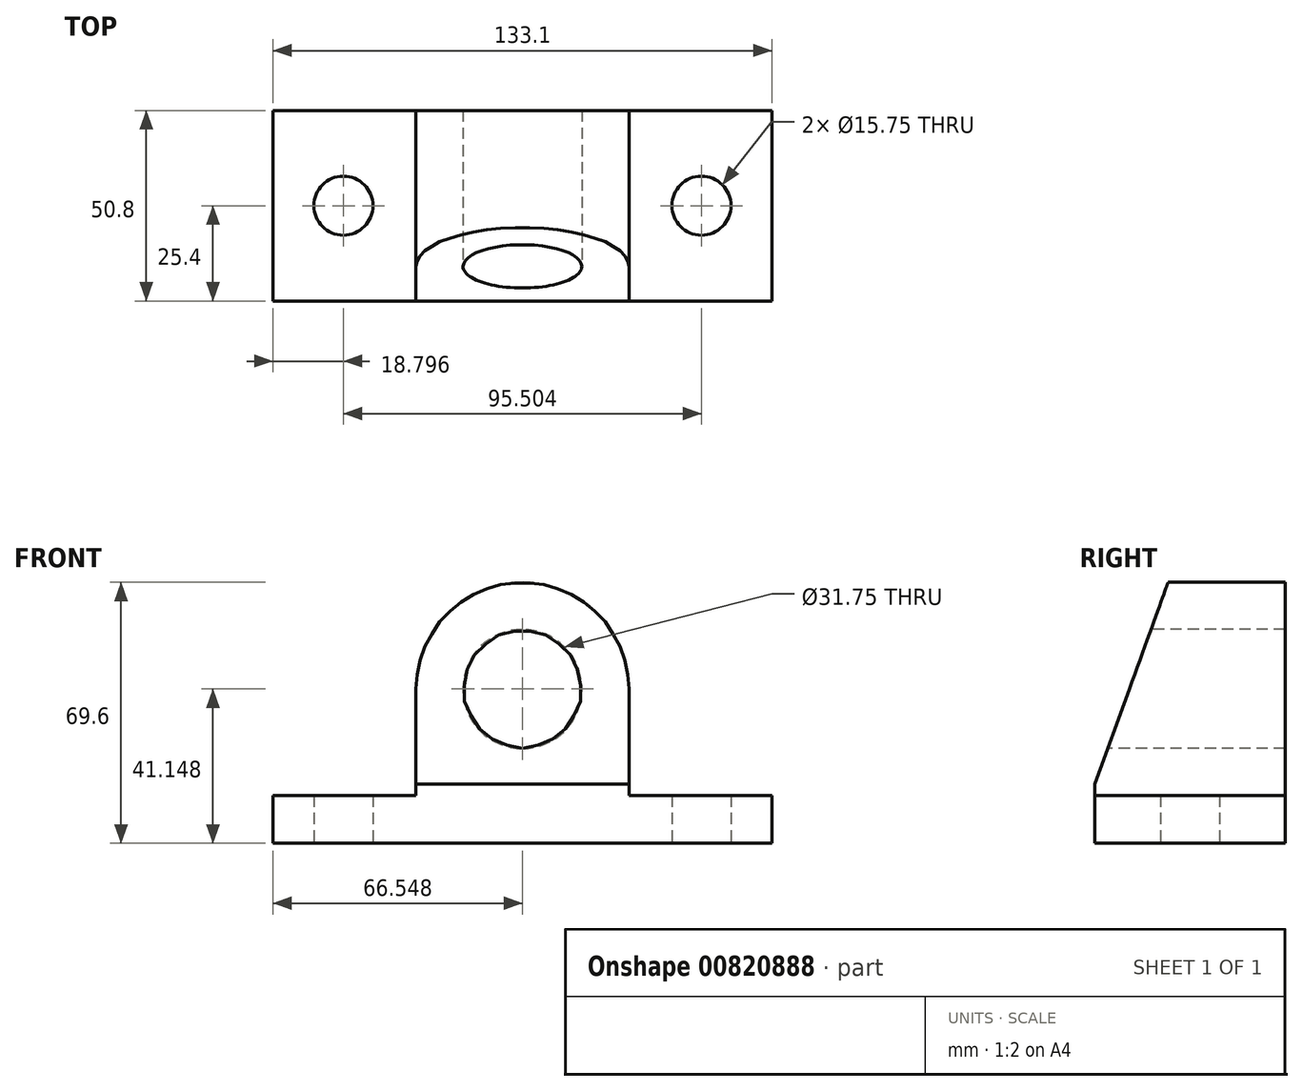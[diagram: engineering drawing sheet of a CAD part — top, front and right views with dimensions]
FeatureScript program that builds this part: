
annotation { "Feature Type Name" : "Feature", "Feature Type Description" : "" }
export const myFeature = defineFeature(function(context is Context, id is Id, definition is map)
    precondition{}
    {
        {
            var Q0;
            Q0=qCreatedBy(makeId("Top.planeOp"),FACE);
            var sketch = newSketch(context, id + "F0", { "sketchPlane" : qUnion([Q0])});
            skLineSegment(sketch, "E0.bottom", {"start": v(0, 0) * mm, "end": v(133.1, 0) * mm});
            skLineSegment(sketch, "E0.top", {"start": v(0, 50.8) * mm, "end": v(133.1, 50.8) * mm});
            skLineSegment(sketch, "E0.left", {"start": v(0, 0) * mm, "end": v(0, 50.8) * mm});
            skLineSegment(sketch, "E0.right", {"start": v(133.1, 0) * mm, "end": v(133.1, 50.8) * mm});
            skLineSegment(sketch, "E1", {"start": v(0, 50.8) * mm, "end": v(66.55, 50.8) * mm});
            skCircle(sketch, "E2", {"center": v(18.8, 25.4) * mm, "radius": 7.87 * mm});
            skCircle(sketch, "E3", {"center": v(114.3, 25.4) * mm, "radius": 7.87 * mm});
            skPoint(sketch, "E4.end.orphan", {"position": v(66.55, 0) * mm});
            skPoint(sketch, "E4.start.orphan", {"position": v(66.55, 25.4) * mm});
            skSolve(sketch);
        }
        {
            var Q0;
            Q0=makeQuery(id+"F0.imprint","IMPRINT",FACE,{"disambiguationData":[TD([[makeQuery(id+"F0.imprint","IMPRINT",EDGE,{"derivedFrom":sQuery(id+"F0.wireOp",EDGE,"E0.bottom")}),1.0]])]});
            extrude(context, id + "F1", {"entities" : qUnion([Q0]), "depth" : 152.4 * mm, "offsetDistance" : 25.4 * mm});
        }
        {
            var Q0;
            Q0=makeQuery(id+"F1.opExtrude","SWEPT_FACE",FACE,{"disambiguationData":[OSD([sQuery(id+"F0.wireOp",EDGE,"E0.bottom")])]});
            var sketch = newSketch(context, id + "F2", { "sketchPlane" : qUnion([Q0])});
            skLineSegment(sketch, "E5", {"start": v(0, 0) * mm, "end": v(0, 12.7) * mm});
            skLineSegment(sketch, "E6", {"start": v(0, 12.7) * mm, "end": v(133.1, 12.7) * mm});
            skLineSegment(sketch, "E7", {"start": v(133.1, 12.7) * mm, "end": v(133.1, 0) * mm});
            skCircle(sketch, "E8", {"center": v(66.55, 41.15) * mm, "radius": 15.88 * mm});
            skLineSegment(sketch, "E9", {"start": v(38.1, 41.15) * mm, "end": v(38.1, 12.7) * mm});
            skLineSegment(sketch, "E10", {"start": v(95, 41.15) * mm, "end": v(95, 12.7) * mm});
            skLineSegment(sketch, "E11", {"start": v(38.1, 12.7) * mm, "end": v(38.1, 15.75) * mm});
            skLineSegment(sketch, "E12", {"start": v(38.1, 15.75) * mm, "end": v(95, 15.75) * mm});
            skArc(sketch, "E13.trimOffspring", {"start": v(95, 41.15) * mm, "mid": v(66.55, 69.6) * mm, "end": v(38.1, 41.15) * mm});
            skPoint(sketch, "E14.start.orphan", {"position": v(66.55, 12.7) * mm});
            skSolve(sketch);
        }
        {
            var Q0;
            Q0=makeQuery(id+"F2.imprint","IMPRINT",FACE,{"disambiguationData":[TD([[makeQuery(id+"F2.imprint","IMPRINT",EDGE,{"derivedFrom":sQuery(id+"F2.wireOp",EDGE,"E9")}),-1.0]])]});
            var Q1;
            Q1=makeQuery(id+"F2.imprint","IMPRINT",FACE,{"disambiguationData":[TD([[makeQuery(id+"F2.imprint","IMPRINT",EDGE,{"derivedFrom":sQuery(id+"F2.wireOp",EDGE,"E8")}),1.0]])]});
            extrude(context, id + "F3", {"entities" : qUnion([Q0, Q1]), "operationType" : NewBodyOperationType.REMOVE, "oppositeDirection" : true, "depth" : 173.74 * mm, "offsetDistance" : 25.4 * mm});
        }
        {
            var Q0;
            Q0=qCreatedBy(makeId("Right.planeOp"),FACE);
            var sketch = newSketch(context, id + "F4", { "sketchPlane" : qUnion([Q0])});
            skLineSegment(sketch, "E15", {"start": v(0, 0) * mm, "end": v(0, 15.75) * mm});
            skLineSegment(sketch, "E16", {"start": v(0, 15.75) * mm, "end": v(0, 77.28) * mm});
            skLineSegment(sketch, "E17", {"start": v(0, 15.75) * mm, "end": v(22.44, 77.4) * mm});
            skLineSegment(sketch, "E18", {"start": v(0, 77.28) * mm, "end": v(22.44, 77.4) * mm});
            skSolve(sketch);
        }
        {
            var Q0;
            Q0=makeQuery(id+"F4.imprint","IMPRINT",FACE,{"disambiguationData":[TD([[makeQuery(id+"F4.imprint","IMPRINT",EDGE,{"derivedFrom":sQuery(id+"F4.wireOp",EDGE,"E16")}),-1.0]])]});
            extrude(context, id + "F5", {"entities" : qUnion([Q0]), "operationType" : NewBodyOperationType.REMOVE, "depth" : 186.44 * mm, "offsetDistance" : 25.4 * mm});
        }
    });
